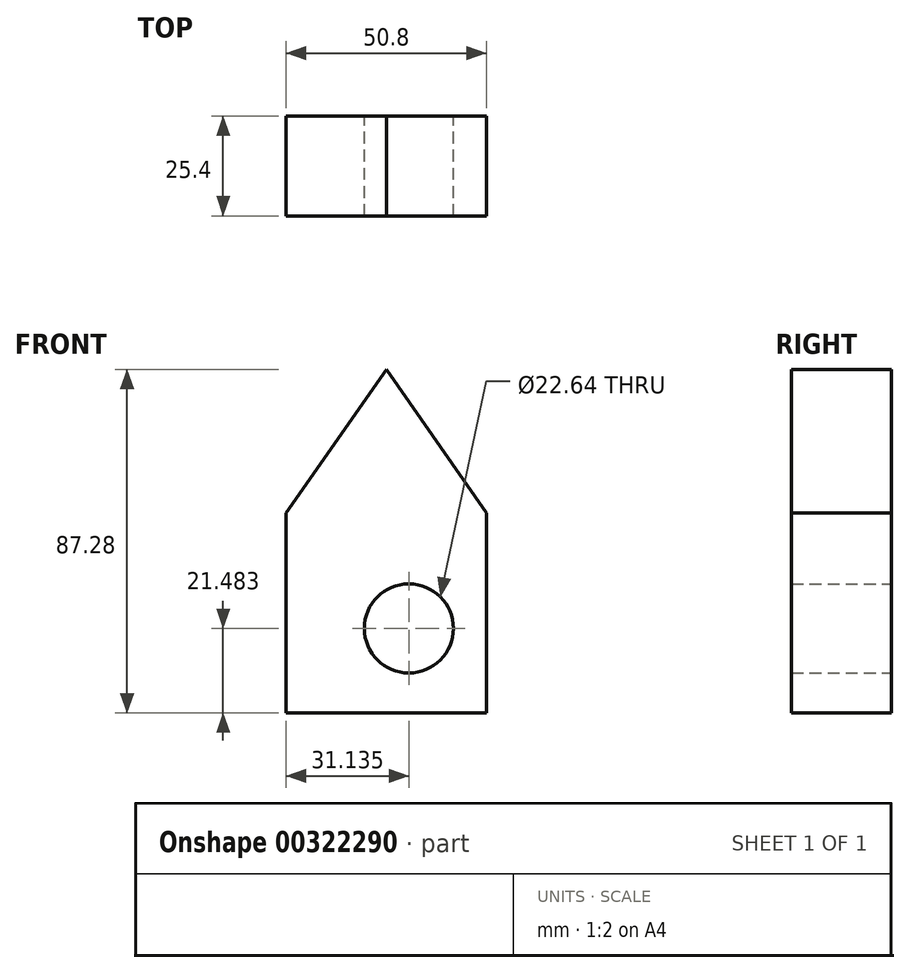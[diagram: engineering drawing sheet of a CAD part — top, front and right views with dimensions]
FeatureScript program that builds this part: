
annotation { "Feature Type Name" : "Feature", "Feature Type Description" : "" }
export const myFeature = defineFeature(function(context is Context, id is Id, definition is map)
    precondition{}
    {
        {
            var Q0;
            Q0=qCreatedBy(makeId("Front.planeOp"),FACE);
            var sketch = newSketch(context, id + "F0", { "sketchPlane" : qUnion([Q0])});
            skLineSegment(sketch, "E0.bottom", {"start": v(25.4, -25.4) * mm, "end": v(-25.4, -25.4) * mm});
            skLineSegment(sketch, "E0.top", {"start": v(25.4, 25.4) * mm, "end": v(-25.4, 25.4) * mm});
            skLineSegment(sketch, "E0.left", {"start": v(25.4, -25.4) * mm, "end": v(25.4, 25.4) * mm});
            skLineSegment(sketch, "E0.right", {"start": v(-25.4, -25.4) * mm, "end": v(-25.4, 25.4) * mm});
            skPoint(sketch, "E0.middle", {"position": v(0, 0) * mm});
            skLineSegment(sketch, "E1", {"start": v(-25.4, 25.4) * mm, "end": v(0, 61.88) * mm});
            skLineSegment(sketch, "E2", {"start": v(25.4, 25.4) * mm, "end": v(0, 61.88) * mm});
            skLineSegment(sketch, "E3", {"start": v(-13.85, 2.38) * mm, "end": v(-13.85, 2.24) * mm});
            skPoint(sketch, "E4.orphan", {"position": v(-13.85, 18.18) * mm});
            skPoint(sketch, "E5.orphan", {"position": v(-17.2, 18.18) * mm});
            skPoint(sketch, "E6.end.orphan", {"position": v(-10.5, 18.18) * mm});
            skPoint(sketch, "E7.orphan", {"position": v(-10.5, 2.24) * mm});
            skLineSegment(sketch, "E8", {"start": v(-12.45, 25.4) * mm, "end": v(-12.45, -25.4) * mm});
            skLineSegment(sketch, "E9", {"start": v(-25.4, -14.55) * mm, "end": v(-12.45, -14.55) * mm});
            skCircle(sketch, "E10", {"center": v(5.73, -3.92) * mm, "radius": 11.32 * mm});
            skSolve(sketch);
        }
        {
            var Q0;
            Q0 = qSketchRegion(id + "F0", true);
            extrude(context, id + "F1", {"entities" : qUnion([Q0]), "depth" : 25.4 * mm});
        }
    });
